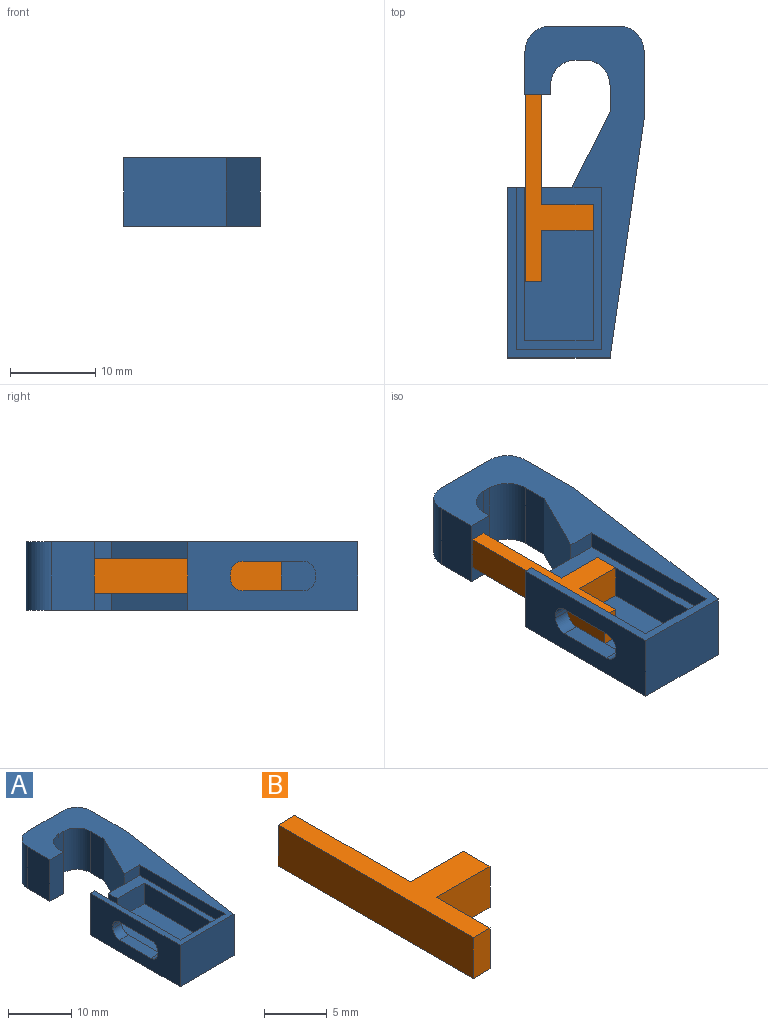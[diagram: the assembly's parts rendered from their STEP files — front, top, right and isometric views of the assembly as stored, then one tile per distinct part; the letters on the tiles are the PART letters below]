
ASSEMBLY  parts=2 mates=1
PART A: 37 faces, bbox 16x39x8 mm
  f0: plane 4x2mm, normal (-1,0,0), area 8mm2, adj f5,f6,f19,f24
  f1: plane 39x16mm, normal (0,0,1), area 222mm2, adj f6,f8,f9,f10,f11,f12,f13,f14
  f2: plane 18x4mm, normal (1,0,0), area 38.9mm2, adj f3,f6,f19,f24,f25,f26,f27,f28
  f3: plane 8x4mm, normal (0,1,0), area 32mm2, adj f2,f4,f19,f24
  f4: plane 16x4mm, normal (-1,0,0), area 64mm2, adj f3,f5,f19,f24
  f5: plane 6x4mm, normal (0,-1,0), area 24mm2, adj f0,f4,f19,f24
  f6: plane 8x7.53mm, normal (0,1,0), area 39.2mm2, adj f0,f1,f2,f7,f17,f18,f19,f21
  f7: plane 39x16mm, normal (0,0,-1), area 412mm2, adj f6,f8,f9,f10,f11,f12,f13,f14
  f8: plane 12x8mm, normal (0,-1,0), area 96mm2, adj f1,f7,f9,f18
  f9: plane 27.99x8mm, normal (0.99,-0.14,0), area 226.2mm2, adj f1,f7,f8,f10
  f10: plane 8.01x8mm, normal (1,0,0), area 64.1mm2, adj f1,f7,f9,f33
  f11: plane 8x8mm, normal (0,1,0), area 64mm2, adj f1,f7,f33,f34
  f12: plane 8x5mm, normal (-1,0,0), area 40mm2, adj f1,f7,f13,f34
  f13: plane 8x3mm, normal (0,-1,0), area 24mm2, adj f1,f7,f12,f14
  f14: plane 8x1mm, normal (1,0,0), area 8mm2, adj f1,f7,f13,f35
  f15: plane 8x1mm, normal (0,-1,0), area 8mm2, adj f1,f7,f35,f36
  f16: plane 8x3.07mm, normal (-1,0,0), area 24.5mm2, adj f1,f7,f17,f36
  f17: plane 8.93x8mm, normal (-0.89,0.45,0), area 79.9mm2, adj f1,f6,f7,f16,f20
  f18: plane 20x8mm, normal (-1,0,0), area 126.9mm2, adj f1,f6,f7,f8,f25,f26,f27,f28
  f19: plane 18x8mm, normal (0,0,1), area 132mm2, adj f0,f2,f3,f4,f5,f6
  f20: plane 3.47x2mm, normal (0,-1,0), area 6.9mm2, adj f1,f17,f23,f24
  f21: plane 19x2mm, normal (1,0,0), area 38mm2, adj f1,f6,f22,f24
  f22: plane 10x2mm, normal (0,1,0), area 20mm2, adj f1,f21,f23,f24
  f23: plane 19x2mm, normal (-1,0,0), area 38mm2, adj f1,f20,f22,f24
  f24: plane 19x10mm, normal (0,0,1), area 58mm2, adj f0,f2,f3,f4,f5,f6,f20,f21
  f25: plane 2x0.5mm, normal (0,-1,0), area 1mm2, adj f2,f18,f26,f32
  f26: cylinder r=1.5mm len=2mm, axis (-1,0,0), area 4.7mm2, adj f2,f18,f25,f27
  f27: plane 7x2mm, normal (0,0,1), area 14mm2, adj f2,f18,f26,f28
  f28: cylinder r=1.5mm len=2mm, axis (-1,0,0), area 4.7mm2, adj f2,f18,f27,f29
  f29: plane 2x0.5mm, normal (0,1,0), area 1mm2, adj f2,f18,f28,f30
  f30: cylinder r=1.5mm len=2mm, axis (-1,0,0), area 4.7mm2, adj f2,f18,f29,f31
  f31: plane 7x2mm, normal (0,0,-1), area 14mm2, adj f2,f18,f30,f32
  f32: cylinder r=1.5mm len=2mm, axis (-1,0,0), area 4.7mm2, adj f2,f18,f25,f31
  f33: cylinder r=3mm len=8mm, axis (0,0,1), area 37.7mm2, adj f1,f7,f10,f11
  f34: cylinder r=3mm len=8mm, axis (0,0,-1), area 37.7mm2, adj f1,f7,f11,f12
  f35: cylinder r=3mm len=8mm, axis (0,0,1), area 37.7mm2, adj f1,f7,f14,f15
  f36: cylinder r=3mm len=8mm, axis (0,0,1), area 37.7mm2, adj f1,f7,f15,f16
PART B: 10 faces, bbox 7.9x22x4 mm
  f0: plane 13x4mm, normal (1,0,0), area 52mm2, adj f1,f7,f8,f9
  f1: plane 4x1.9mm, normal (0,1,0), area 7.6mm2, adj f0,f2,f8,f9
  f2: plane 22x4mm, normal (-1,0,0), area 88mm2, adj f1,f3,f8,f9
  f3: plane 4x1.9mm, normal (0,-1,0), area 7.6mm2, adj f2,f4,f8,f9
  f4: plane 6x4mm, normal (1,0,0), area 24mm2, adj f3,f5,f8,f9
  f5: plane 6x4mm, normal (0,-1,0), area 24mm2, adj f4,f6,f8,f9
  f6: plane 4x3mm, normal (1,0,0), area 12mm2, adj f5,f7,f8,f9
  f7: plane 6x4mm, normal (0,1,0), area 24mm2, adj f0,f6,f8,f9
  f8: plane 22x7.9mm, normal (0,0,1), area 59.8mm2, adj f0,f1,f2,f3,f4,f5,f6,f7
  f9: plane 22x7.9mm, normal (0,0,-1), area 59.8mm2, adj f0,f1,f2,f3,f4,f5,f6,f7
PLACE A t=(0,6.8,0)mm
PLACE B t=(0,6.8,0)mm
MATE slider B.f7 <-> A.f5  axis (0,1,0) through (-2,14.8,4)mm
